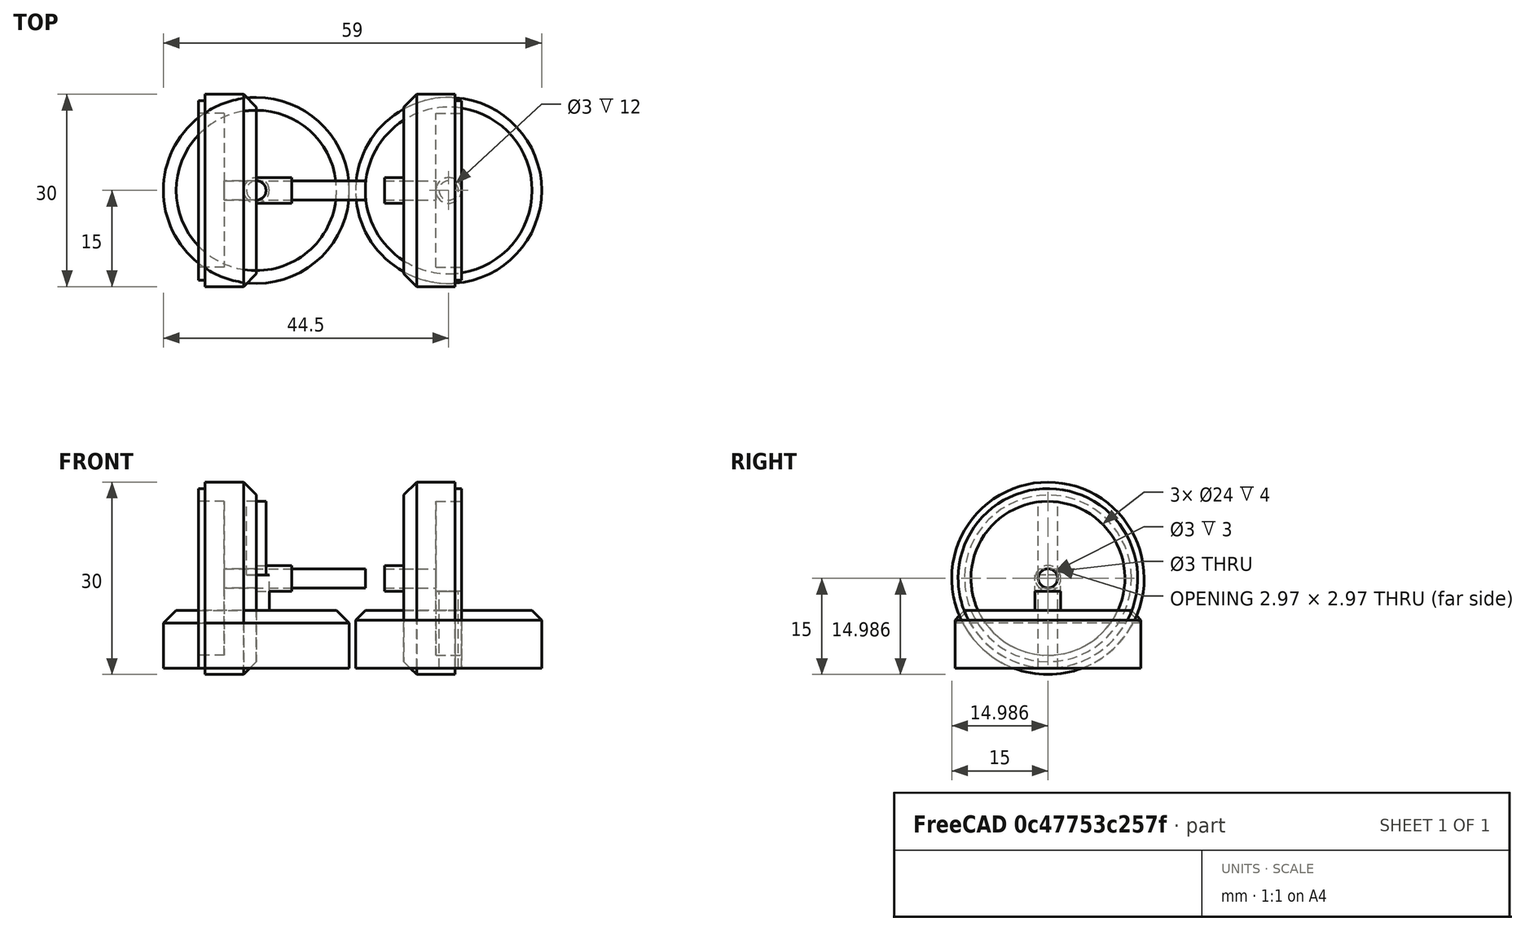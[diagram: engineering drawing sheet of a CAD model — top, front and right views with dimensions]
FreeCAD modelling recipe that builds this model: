
FCSTD DOCUMENT  (FreeCAD 0.18R4 (GitTag))
Label: опорный каток
License: All rights reserved
LicenseURL: http://en.wikipedia.org/wiki/All_rights_reserved
objects: Sketcher::SketchObject×5, PartDesign::Revolution×5, PartDesign::Body×5, Part::Cylinder×4, App::MeasureDistance×4, Mesh::Feature×2, PartDesign::Boolean×1, Part::MultiFuse×1, Part::Cut×1, PartDesign::ShapeBinder×1
note: 28 computed .brp shape members not serialized (recipe doc carries the construction recipe); baked Part::Feature solids carry a one-line shape summary decoded from their .brp

FEATURE [Mesh::Feature] Napravljajushhee_koleso
  Placement = pos=(-9,0,0) rot=(0,0,1;0rad)
FEATURE [Sketcher::SketchObject] Sketch
  MapMode = 5
  Support = -> [XY_Plane]
  sketch-geometry (9):
    g0: LineSegment StartX=0 StartY=1.5 StartZ=0 EndX=0 EndY=13 EndZ=0
    g1: LineSegment StartX=0 StartY=13 StartZ=0 EndX=-2 EndY=15 EndZ=0
    g2: LineSegment StartX=-2 StartY=15 StartZ=0 EndX=-8 EndY=15 EndZ=0
    g3: LineSegment StartX=-8 StartY=15 StartZ=0 EndX=-8 EndY=14 EndZ=0
    g4: LineSegment StartX=-8 StartY=14 StartZ=0 EndX=-9 EndY=14 EndZ=0
    g5: LineSegment StartX=-9 StartY=14 StartZ=0 EndX=-9 EndY=12 EndZ=0
    g6: LineSegment StartX=-5 StartY=1.5 StartZ=0 EndX=-5 EndY=12 EndZ=0
    g7: LineSegment StartX=-5 StartY=12 StartZ=0 EndX=-9 EndY=12 EndZ=0
    g8: LineSegment StartX=0 StartY=1.5 StartZ=0 EndX=-5 EndY=1.5 EndZ=0
  constraints (27):
    c: Coincident(g2,g3)
    c: Coincident(g3,g4)
    c: Coincident(g6,g7)
    c: Parallel(g8,g-1)
    c: Perpendicular(g-1,g6)
    c: Perpendicular(g-1,g0)
    c: Parallel(g2,g-1)
    c: Parallel(g7,g-1)
    c: Perpendicular(g-1,g5)
    c: Parallel(g4,g-1)
    c: Perpendicular(g-1,g3)
    c: Angle(g1,g0) = 2.35619
    c: Coincident(g6,g8)
    c: Coincident(g5,g7)
    c: Coincident(g4,g5)
    c: Coincident(g1,g2)
    c: Coincident(g0,g1)
    c: Coincident(g0,g8)
    c: DistanceX(g5,g0) = 9
    c: Distance(g3) = 1
    c: DistanceX(g-1,g0) = 0
    c: Distance(g8) = 5
    c: Distance(g5) = 2
    c: Distance(g2) = 6
    c: DistanceY(g-1,g0) = 1.5
    c: Distance(g4) = 1
    c: Distance(g6) = 10.5
FEATURE [PartDesign::Revolution] Revolution
  Angle = 360
  Axis = (1,0,0)
  Base = (0,0,0)
  Profile = -> Sketch
  ReferenceAxis = -> Sketch [H_Axis]
FEATURE [PartDesign::Body] Body
  Group = -> [Sketch,Revolution]
  Origin = -> Origin
  Tip = -> Revolution
FEATURE [Mesh::Feature] Trak_WALL_E001  label="Trak_WALL-E001"
  Placement = pos=(23.5,-3,-18) rot=(0,1,0;-1.5708rad)
FEATURE [Sketcher::SketchObject] Sketch001
  MapMode = 5
  Support = -> [XY_Plane001]
  sketch-geometry (9):
    g0: LineSegment StartX=0 StartY=1.5 StartZ=0 EndX=0 EndY=13 EndZ=0
    g1: LineSegment StartX=0 StartY=13 StartZ=0 EndX=-2 EndY=15 EndZ=0
    g2: LineSegment StartX=-2 StartY=15 StartZ=0 EndX=-8 EndY=15 EndZ=0
    g3: LineSegment StartX=-8 StartY=15 StartZ=0 EndX=-8 EndY=14 EndZ=0
    g4: LineSegment StartX=-8 StartY=14 StartZ=0 EndX=-9 EndY=14 EndZ=0
    g5: LineSegment StartX=-9 StartY=14 StartZ=0 EndX=-9 EndY=12 EndZ=0
    g6: LineSegment StartX=-5 StartY=1.5 StartZ=0 EndX=-5 EndY=12 EndZ=0
    g7: LineSegment StartX=-5 StartY=12 StartZ=0 EndX=-9 EndY=12 EndZ=0
    g8: LineSegment StartX=0 StartY=1.5 StartZ=0 EndX=-5 EndY=1.5 EndZ=0
  constraints (27):
    c: Coincident(g2,g3)
    c: Coincident(g3,g4)
    c: Coincident(g6,g7)
    c: Parallel(g8,g-1)
    c: Perpendicular(g-1,g6)
    c: Perpendicular(g-1,g0)
    c: Parallel(g2,g-1)
    c: Parallel(g7,g-1)
    c: Perpendicular(g-1,g5)
    c: Parallel(g4,g-1)
    c: Perpendicular(g-1,g3)
    c: Angle(g1,g0) = 2.35619
    c: Coincident(g6,g8)
    c: Coincident(g5,g7)
    c: Coincident(g4,g5)
    c: Coincident(g1,g2)
    c: Coincident(g0,g1)
    c: Coincident(g0,g8)
    c: DistanceX(g5,g0) = 9
    c: Distance(g3) = 1
    c: DistanceX(g-1,g0) = 0
    c: Distance(g8) = 5
    c: Distance(g5) = 2
    c: Distance(g2) = 6
    c: DistanceY(g-1,g0) = 1.5
    c: Distance(g4) = 1
    c: Distance(g6) = 10.5
FEATURE [PartDesign::Revolution] Revolution001
  Angle = 360
  Axis = (1,0,0)
  Base = (0,0,0)
  Profile = -> Sketch001
  ReferenceAxis = -> Sketch001 [H_Axis]
FEATURE [Part::Cylinder] Cylinder  label="Цилиндр"
  Angle = 360
  AttacherType = Attacher::AttachEngine3D
  Height = 22
  Placement = pos=(-5,0,0) rot=(0,1,0;1.5708rad)
  Radius = 1.5
FEATURE [App::MeasureDistance] Distance002  label="Distance: 12,00 mm"
  Distance = 12.0046
  P1 = (0,2.82883,12.6661)
  P2 = (12,3.15389,12.5911)
FEATURE [Part::Cylinder] Cylinder001  label="Цилиндр001"
  Angle = 360
  AttacherType = Attacher::AttachEngine3D
  Height = 5.5
  Placement = pos=(0,0,0) rot=(0,1,0;1.5708rad)
  Radius = 2
FEATURE [Part::Cylinder] Cylinder002  label="Цилиндр002"
  Angle = 360
  AttacherType = Attacher::AttachEngine3D
  Height = 3
  Placement = pos=(9,0,0) rot=(0,1,0;1.5708rad)
  Radius = 2
FEATURE [PartDesign::Boolean] Boolean
  BaseFeature = -> Revolution001
  Group = -> [Body,Cylinder001,Cylinder]
  Type = 0
FEATURE [Sketcher::SketchObject] Sketch002
  MapMode = 5
  Support = -> [XY_Plane003]
  sketch-geometry (9):
    g0: LineSegment StartX=0 StartY=1.5 StartZ=0 EndX=0 EndY=13 EndZ=0
    g1: LineSegment StartX=0 StartY=13 StartZ=0 EndX=-2 EndY=15 EndZ=0
    g2: LineSegment StartX=-2 StartY=15 StartZ=0 EndX=-8 EndY=15 EndZ=0
    g3: LineSegment StartX=-8 StartY=15 StartZ=0 EndX=-8 EndY=14 EndZ=0
    g4: LineSegment StartX=-8 StartY=14 StartZ=0 EndX=-9 EndY=14 EndZ=0
    g5: LineSegment StartX=-9 StartY=14 StartZ=0 EndX=-9 EndY=12 EndZ=0
    g6: LineSegment StartX=-5 StartY=1.5 StartZ=0 EndX=-5 EndY=12 EndZ=0
    g7: LineSegment StartX=-5 StartY=12 StartZ=0 EndX=-9 EndY=12 EndZ=0
    g8: LineSegment StartX=0 StartY=1.5 StartZ=0 EndX=-5 EndY=1.5 EndZ=0
  constraints (27):
    c: Coincident(g2,g3)
    c: Coincident(g3,g4)
    c: Coincident(g6,g7)
    c: Parallel(g8,g-1)
    c: Perpendicular(g-1,g6)
    c: Perpendicular(g-1,g0)
    c: Parallel(g2,g-1)
    c: Parallel(g7,g-1)
    c: Perpendicular(g-1,g5)
    c: Parallel(g4,g-1)
    c: Perpendicular(g-1,g3)
    c: Angle(g1,g0) = 2.35619
    c: Coincident(g6,g8)
    c: Coincident(g5,g7)
    c: Coincident(g4,g5)
    c: Coincident(g1,g2)
    c: Coincident(g0,g1)
    c: Coincident(g0,g8)
    c: DistanceX(g5,g0) = 9
    c: Distance(g3) = 1
    c: DistanceX(g-1,g0) = 0
    c: Distance(g8) = 5
    c: Distance(g5) = 2
    c: Distance(g2) = 6
    c: DistanceY(g-1,g0) = 1.5
    c: Distance(g4) = 1
    c: Distance(g6) = 10.5
FEATURE [PartDesign::Revolution] Revolution002
  Angle = 360
  Axis = (1,0,0)
  Base = (0,0,0)
  Profile = -> Sketch002
  ReferenceAxis = -> Sketch002 [H_Axis]
FEATURE [PartDesign::Body] Body002
  Group = -> [Revolution002,Sketch002]
  Origin = -> Origin002
  Placement = pos=(12,0,0) rot=(0,0,1;3.14159rad)
  Tip = -> Revolution002
FEATURE [Part::MultiFuse] Fusion
  Placement = pos=(11,0,0) rot=(0,0,1;0rad)
  Shapes = -> [Cylinder002,Body002]
FEATURE [Part::Cylinder] Cylinder003  label="Цилиндр003"
  Angle = 360
  AttacherType = Attacher::AttachEngine3D
  Height = 22
  Placement = pos=(18,0,0) rot=(0,1,0;1.5708rad)
  Radius = 1.5
FEATURE [Part::Cut] Cut
  Base = -> Fusion
  Tool = -> Cylinder003
FEATURE [App::MeasureDistance] Distance003  label="Distance: 3,50 mm"
  Distance = 3.50255
  P1 = (5.5,0.133585,1.99553)
  P2 = (9,2e-15,2)
FEATURE [App::MeasureDistance] Distance  label="Distance: 2,98 mm"
  Distance = 2.98241
  P1 = (28,0.0354366,-1.49558)
  P2 = (28,0.0780251,1.48653)
FEATURE [App::MeasureDistance] Distance004  label="Distance: 2,98 mm001"
  Distance = 2.97813
  P1 = (17,0.358974,1.45641)
  P2 = (17,0,-1.5)
FEATURE [Sketcher::SketchObject] Sketch003
  MapMode = 5
  Support = -> [XY_Plane004]
  sketch-geometry (11):
    g0: LineSegment StartX=0 StartY=2 StartZ=0 EndX=0 EndY=12.5 EndZ=0
    g1: LineSegment StartX=0 StartY=12.5 StartZ=0 EndX=-2 EndY=14.5 EndZ=0
    g2: LineSegment StartX=-2 StartY=14.5 StartZ=0 EndX=-9 EndY=14.5 EndZ=0
    g3: LineSegment StartX=-9 StartY=14.5 StartZ=0 EndX=-9 EndY=13.5 EndZ=0
    g4: LineSegment StartX=-9 StartY=13.5 StartZ=0 EndX=-9 EndY=11.5 EndZ=0
    g5: LineSegment StartX=-9 StartY=0 StartZ=0 EndX=-9 EndY=11.5 EndZ=0
    g6: LineSegment StartX=0 StartY=2 StartZ=0 EndX=5.5 EndY=2 EndZ=0
    g7: LineSegment StartX=17 StartY=0 StartZ=0 EndX=-9 EndY=0 EndZ=0
    g8: LineSegment StartX=5.5 StartY=2 StartZ=0 EndX=5.5 EndY=1.52 EndZ=0
    g9: LineSegment StartX=5.5 StartY=1.52 StartZ=0 EndX=17 EndY=1.52 EndZ=0
    g10: LineSegment StartX=17 StartY=1.52 StartZ=0 EndX=17 EndY=0 EndZ=0
  constraints (33):
    c: Coincident(g2,g3)
    c: Perpendicular(g-1,g5)
    c: Perpendicular(g-1,g0)
    c: Parallel(g2,g-1)
    c: Perpendicular(g-1,g4)
    c: Perpendicular(g-1,g3)
    c: Angle(g1,g0) = 2.35619
    c: Coincident(g1,g2)
    c: Coincident(g0,g1)
    c: DistanceX(g4,g0) = 9
    c: Distance(g3) = 1
    c: Distance(g4) = 2
    c: Distance(g2) = 7
    c: Distance(g5) = 11.5
    c: Coincident(g4,g5)
    c: PointOnObject(g0,g-2)
    c: PointOnObject(g5,g-1)
    c: DistanceY(g-1,g0) = 2
    c: Coincident(g5,g7)
    c: Coincident(g0,g6)
    c: Parallel(g6,g7)
    c: Parallel(g7,g-1)
    c: Distance(g6) = 5.5
    c: Coincident(g8,g9)
    c: Coincident(g9,g10)
    c: Coincident(g6,g8)
    c: Parallel(g0,g8)
    c: Parallel(g10,g0)
    c: Coincident(g7,g10)
    c: Parallel(g9,g7)
    c: Distance(g10) = 1.52
    c: Distance(g7) = 26
    c: Coincident(g3,g4)
FEATURE [PartDesign::ShapeBinder] ReferenceSketch003
  Support = -> [Sketch003]
  TraceSupport = false
FEATURE [PartDesign::Body] Body001
  Group = -> [Sketch001,Revolution001,Boolean,ReferenceSketch003]
  Origin = -> Origin001
  Tip = -> Boolean
FEATURE [PartDesign::Revolution] Revolution003
  Angle = 360
  Axis = (1,0,0)
  Base = (0,0,0)
  Profile = -> Sketch003
  ReferenceAxis = -> Sketch003 [H_Axis]
FEATURE [PartDesign::Body] Body003
  Group = -> [Sketch003,Revolution003]
  Origin = -> Origin003
  Placement = pos=(1.1e-15,0,-5) rot=(0,1,0;4.71239rad)
  Tip = -> Revolution003
FEATURE [Sketcher::SketchObject] Sketch004
  MapMode = 5
  Support = -> [XY_Plane006]
  sketch-geometry (9):
    g0: LineSegment StartX=0 StartY=2 StartZ=0 EndX=0 EndY=13 EndZ=0
    g1: LineSegment StartX=0 StartY=13 StartZ=0 EndX=-1.5 EndY=14.5 EndZ=0
    g2: LineSegment StartX=-1.5 StartY=14.5 StartZ=0 EndX=-9 EndY=14.5 EndZ=0
    g3: LineSegment StartX=-9 StartY=14.5 StartZ=0 EndX=-9 EndY=13.5 EndZ=0
    g4: LineSegment StartX=-9 StartY=13.5 StartZ=0 EndX=-9 EndY=11.5 EndZ=0
    g5: LineSegment StartX=-9 StartY=1.5 StartZ=0 EndX=-9 EndY=11.5 EndZ=0
    g6: LineSegment StartX=0 StartY=2 StartZ=0 EndX=3 EndY=2 EndZ=0
    g7: LineSegment StartX=3 StartY=2 StartZ=0 EndX=3 EndY=1.5 EndZ=0
    g8: LineSegment StartX=-9 StartY=1.5 StartZ=0 EndX=3 EndY=1.5 EndZ=0
  constraints (27):
    c: Coincident(g2,g3)
    c: Perpendicular(g-1,g5)
    c: Perpendicular(g-1,g0)
    c: Parallel(g2,g-1)
    c: Perpendicular(g-1,g4)
    c: Perpendicular(g-1,g3)
    c: Angle(g1,g0) = 2.35619
    c: Coincident(g1,g2)
    c: Coincident(g0,g1)
    c: DistanceX(g4,g0) = 9
    c: Distance(g3) = 1
    c: DistanceX(g-1,g0) = 0
    c: Distance(g4) = 2
    c: Distance(g5) = 10
    c: Coincident(g3,g4)
    c: Coincident(g4,g5)
    c: DistanceY(g-1,g5) = 1.5
    c: Distance(g0) = 11
    c: Coincident(g0,g6)
    c: Coincident(g6,g7)
    c: Coincident(g5,g8)
    c: Coincident(g7,g8)
    c: Parallel(g8,g-1)
    c: Parallel(g7,g0)
    c: Parallel(g6,g8)
    c: Distance(g6) = 3
    c: Distance(g2) = 7.5
FEATURE [PartDesign::Revolution] Revolution004
  Angle = 360
  Axis = (1,0,0)
  Base = (0,0,0)
  Profile = -> Sketch004
  ReferenceAxis = -> Sketch004 [H_Axis]
FEATURE [PartDesign::Body] Body004
  Group = -> [Sketch004,Revolution004]
  Origin = -> Origin004
  Placement = pos=(30,0,-5) rot=(-0.707107,0,-0.707107;3.14159rad)
  Tip = -> Revolution004
